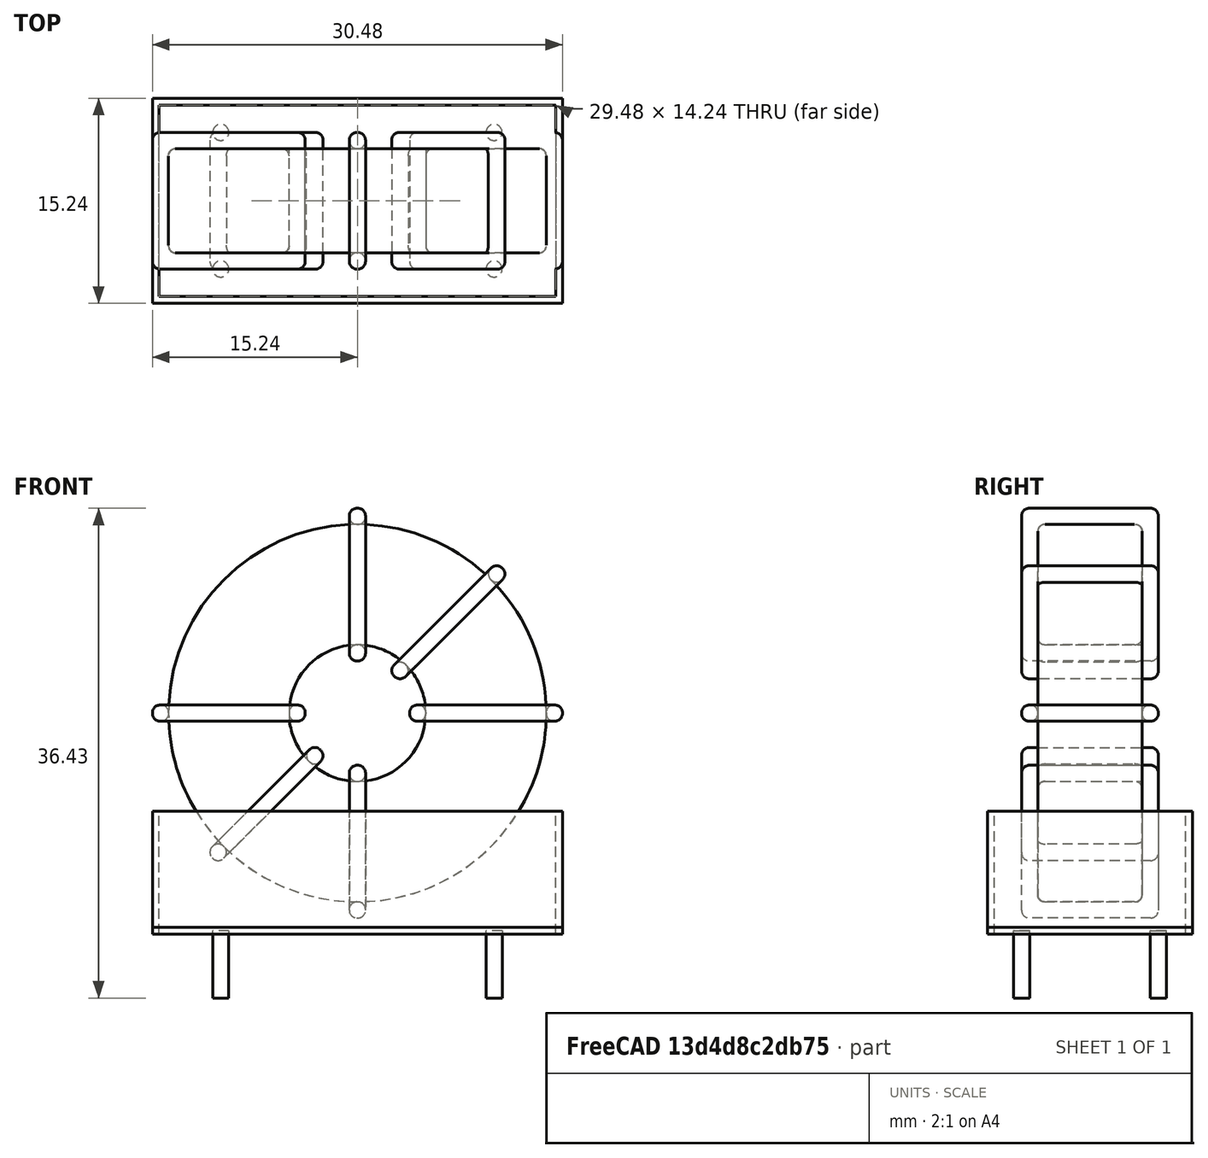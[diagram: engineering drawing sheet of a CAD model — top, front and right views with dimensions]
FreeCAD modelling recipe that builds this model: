
FCSTD DOCUMENT  (FreeCAD 0.16R6703 (Git))
Label: L_CommonModeChoke_Toroid_Vertical_L30.5mm_W15.2mm_Px10.16mm_Py20.32mm_Bourns_8100series
License: All rights reserved
LicenseURL: http://en.wikipedia.org/wiki/All_rights_reserved
objects: Sketcher::SketchObject×8, PartDesign::Pad×8, PartDesign::Fillet×5, Spreadsheet::Sheet×1
note: 29 computed .brp shape members not serialized (recipe doc carries the construction recipe); baked Part::Feature solids carry a one-line shape summary decoded from their .brp

FEATURE [Spreadsheet::Sheet] Spreadsheet  label="dimensions"
  cells = A1=Wx; B1(Wx)=30.48; C1(WW)=10.16; D1(iWx)=30.48; A2=Wy; B2(Wy)=10.16; D2(iWy)=15.24; A3=RM; B3(RMx)=10.16; C3(RMy)=20.32; A4=d_wire; B4(d_wire)=1.2; A5=H; B5(H)=31; A6=offsetx; B6(offsetx)=5.079999999999998
FEATURE [Sketcher::SketchObject] Sketch
  Placement = pos=(10.16,-5.08,0) rot=(1,0,0;1.5708rad)
  expr: Placement.Base.x = Spreadsheet.RMy / 2
  expr: Constraints[4] = Spreadsheet.WW / 2
  expr: Placement.Base.y = -Spreadsheet.RMx / 2
  expr: Constraints[0] = Spreadsheet.Wx / 2 - Spreadsheet.d_wire
  expr: Constraints[2] = Spreadsheet.Wx / 2 + Spreadsheet.d_wire + 0.5
  sketch-geometry (2):
    g0: Circle CenterX=0 CenterY=16.94 CenterZ=0 NormalX=0 NormalY=0 NormalZ=1 Radius=14.04
    g1: Circle CenterX=0 CenterY=16.94 CenterZ=0 NormalX=0 NormalY=0 NormalZ=1 Radius=5.08
  constraints (5):
    c: Radius(g0) = 14.04
    c: DistanceX(g-1,g0) = 0
    c: DistanceY(g-1,g0) = 16.94
    c: Coincident(g1,g0)
    c: Radius(g1) = 5.08
FEATURE [PartDesign::Pad] Pad
  Length = 7.76
  Length2 = 100
  Midplane = true
  Placement = pos=(10.16,-5.08,0) rot=(1,0,0;1.5708rad)
  Sketch = -> Sketch
  Type = 0
  expr: Length = Spreadsheet.Wy - 2 * Spreadsheet.d_wire
FEATURE [Sketcher::SketchObject] Sketch001
  Placement = pos=(0,0,0.75) rot=(0,0,1;0rad)
  expr: Constraints[4] = Spreadsheet.RMy
  expr: Constraints[2] = -Spreadsheet.RMx
  expr: Constraints[1] = Spreadsheet.d_wire / 2
  sketch-geometry (4):
    g0: Circle CenterX=0 CenterY=0 CenterZ=0 NormalX=0 NormalY=0 NormalZ=1 Radius=0.6
    g1: Circle CenterX=20.32 CenterY=-10.16 CenterZ=0 NormalX=0 NormalY=0 NormalZ=1 Radius=0.6
    g2: Circle CenterX=0 CenterY=-10.16 CenterZ=0 NormalX=0 NormalY=0 NormalZ=1 Radius=0.6
    g3: Circle CenterX=20.32 CenterY=0 CenterZ=0 NormalX=0 NormalY=0 NormalZ=1 Radius=0.6
  constraints (11):
    c: Equal(g0,g1)
    c: Radius(g0) = 0.6
    c: DistanceY(g-1,g1) = -10.16
    c: Coincident(g0,g-1)
    c: DistanceX(g-1,g1) = 20.32
    c: PointOnObject(g2,g-2)
    c: DistanceY(g-1,g3) = 0
    c: DistanceY(g2,g1) = 0
    c: DistanceX(g3,g1) = 0
    c: Equal(g3,g2)
    c: Equal(g2,g1)
FEATURE [PartDesign::Pad] Pad001
  Length = 5
  Length2 = 0
  Placement = pos=(0,0,0.75) rot=(0,0,1;0rad)
  Reversed = true
  Sketch = -> Sketch001
  Type = 0
FEATURE [PartDesign::Fillet] Fillet
  Base = -> Pad [Edge6,Edge3,Edge2]
  Placement = pos=(10.16,-5.08,0) rot=(1,0,0;1.5708rad)
  Radius = 0.5
FEATURE [Sketcher::SketchObject] Sketch003
  Placement = pos=(10.16,0,16.94) rot=(1,0,0;3.14159rad)
  expr: Placement.Base.x = Spreadsheet.RMy / 2
  expr: Constraints[18] = Spreadsheet.d_wire
  expr: Constraints[16] = Spreadsheet.d_wire
  expr: Constraints[19] = Spreadsheet.d_wire
  expr: Constraints[17] = Spreadsheet.d_wire
  expr: Placement.Base.y = -1 * (Spreadsheet.RMx - Spreadsheet.Wy) / 2
  expr: Constraints[21] = (Spreadsheet.Wx - Spreadsheet.WW) / 2 - Spreadsheet.d_wire
  expr: Constraints[22] = Spreadsheet.Wx / 2 - Spreadsheet.d_wire
  expr: Constraints[43] = Spreadsheet.d_wire
  expr: Constraints[48] = Spreadsheet.Wx - Spreadsheet.d_wire * 2
  expr: Constraints[49] = Spreadsheet.Wy
  expr: Placement.Base.z = Spreadsheet.Wx / 2 + Spreadsheet.d_wire + 0.5
  sketch-geometry (16):
    g0: LineSegment StartX=-3.88 StartY=0 StartZ=0 EndX=-15.24 EndY=0 EndZ=0
    g1: LineSegment StartX=-15.24 StartY=0 StartZ=0 EndX=-15.24 EndY=10.16 EndZ=0
    g2: LineSegment StartX=-15.24 StartY=10.16 StartZ=0 EndX=-3.88 EndY=10.16 EndZ=0
    g3: LineSegment StartX=-3.88 StartY=10.16 StartZ=0 EndX=-3.88 EndY=0 EndZ=0
    g4: LineSegment StartX=-14.04 StartY=8.96 StartZ=0 EndX=-5.08 EndY=8.96 EndZ=0
    g5: LineSegment StartX=-5.08 StartY=8.96 StartZ=0 EndX=-5.08 EndY=1.2 EndZ=0
    g6: LineSegment StartX=-5.08 StartY=1.2 StartZ=0 EndX=-14.04 EndY=1.2 EndZ=0
    g7: LineSegment StartX=-14.04 StartY=1.2 StartZ=0 EndX=-14.04 EndY=8.96 EndZ=0
    g8: LineSegment StartX=3.88 StartY=10.16 StartZ=0 EndX=15.24 EndY=10.16 EndZ=0
    g9: LineSegment StartX=15.24 StartY=10.16 StartZ=0 EndX=15.24 EndY=0 EndZ=0
    g10: LineSegment StartX=15.24 StartY=0 StartZ=0 EndX=3.88 EndY=0 EndZ=0
    g11: LineSegment StartX=3.88 StartY=0 StartZ=0 EndX=3.88 EndY=10.16 EndZ=0
    g12: LineSegment StartX=5.08 StartY=8.96 StartZ=0 EndX=14.04 EndY=8.96 EndZ=0
    g13: LineSegment StartX=14.04 StartY=8.96 StartZ=0 EndX=14.04 EndY=1.2 EndZ=0
    g14: LineSegment StartX=14.04 StartY=1.2 StartZ=0 EndX=5.08 EndY=1.2 EndZ=0
    g15: LineSegment StartX=5.08 StartY=1.2 StartZ=0 EndX=5.08 EndY=8.96 EndZ=0
  constraints (50):
    c: Horizontal(g0)
    c: Coincident(g1,g0)
    c: Vertical(g1)
    c: Coincident(g2,g1)
    c: Horizontal(g2)
    c: Coincident(g3,g2)
    c: Coincident(g3,g0)
    c: Vertical(g3)
    c: Coincident(g4,g5)
    c: Coincident(g5,g6)
    c: Coincident(g6,g7)
    c: Coincident(g7,g4)
    c: Horizontal(g4)
    c: Horizontal(g6)
    c: Vertical(g5)
    c: Vertical(g7)
    c: DistanceX(g1,g4) = 1.2
    c: DistanceY(g4,g1) = 1.2
    c: DistanceX(g5,g0) = 1.2
    c: DistanceY(g0,g5) = 1.2
    c: DistanceY(g-1,g0) = 0
    c: DistanceX(g6,g6) = 8.96
    c: DistanceX(g6,g-1) = 14.04
    c: Coincident(g8,g9)
    c: Coincident(g9,g10)
    c: Coincident(g10,g11)
    c: Coincident(g11,g8)
    c: Horizontal(g8)
    c: Horizontal(g10)
    c: Vertical(g9)
    c: Vertical(g11)
    c: Coincident(g12,g13)
    c: Coincident(g13,g14)
    c: Coincident(g14,g15)
    c: Coincident(g15,g12)
    c: Horizontal(g12)
    c: Horizontal(g14)
    c: Vertical(g13)
    c: Vertical(g15)
    c: DistanceY(g8,g2) = 0
    c: DistanceY(g10,g0) = 0
    c: DistanceY(g14,g5) = 0
    c: DistanceY(g12,g4) = 0
    c: DistanceX(g8,g12) = 1.2
    c: Equal(g8,g2)
    c: Equal(g12,g4)
    c: Equal(g9,g1)
    c: Equal(g13,g7)
    c: DistanceX(g4,g12) = 28.08
    c: DistanceY(g0,g1) = 10.16
FEATURE [PartDesign::Pad] Pad002
  Length = 1.2
  Length2 = 100
  Midplane = true
  Placement = pos=(10.16,0,16.94) rot=(1,0,0;3.14159rad)
  Sketch = -> Sketch003
  Type = 0
  expr: Length = Spreadsheet.d_wire
FEATURE [PartDesign::Fillet] Fillet001
  Base = -> Pad002 [Edge38,Edge41,Edge42,Edge43,Edge29,Edge32,Edge33,Edge34,Edge25,Edge35,Edge36,Edge13,Edge14,Edge15,Edge16,Edge17,Edge18,Edge19,Edge1,Edge2,Edge3,Edge4,Edge5,Edge6,Edge7,Edge37,Edge39,Edge40,Edge20,Edge23,Edge24,Edge21,Edge22,Edge8,Edge9,Edge10,Edge11,Edge12,Edge26,Edge27,+8 more]
  Placement = pos=(10.16,0,16.94) rot=(1,0,0;3.14159rad)
  Radius = 0.564
  expr: Radius = Spreadsheet.d_wire * 0.47
FEATURE [Sketcher::SketchObject] Sketch004
  Placement = pos=(10.16,0,16.94) rot=(0.92388,0,0.382683;3.14159rad)
  expr: Placement.Base.x = Spreadsheet.RMy / 2
  expr: Constraints[18] = Spreadsheet.d_wire
  expr: Constraints[16] = Spreadsheet.d_wire
  expr: Constraints[19] = Spreadsheet.d_wire
  expr: Constraints[17] = Spreadsheet.d_wire
  expr: Placement.Base.y = -1 * (Spreadsheet.RMx - Spreadsheet.Wy) / 2
  expr: Constraints[21] = (Spreadsheet.Wx - Spreadsheet.WW) / 2 - Spreadsheet.d_wire
  expr: Constraints[22] = Spreadsheet.Wx / 2 - Spreadsheet.d_wire
  expr: Constraints[43] = Spreadsheet.d_wire
  expr: Constraints[48] = Spreadsheet.Wx - 2 * Spreadsheet.d_wire
  expr: Constraints[49] = Spreadsheet.Wy
  expr: Placement.Base.z = Spreadsheet.Wx / 2 + Spreadsheet.d_wire + 0.5
  sketch-geometry (16):
    g0: LineSegment StartX=-3.88 StartY=0 StartZ=0 EndX=-15.24 EndY=0 EndZ=0
    g1: LineSegment StartX=-15.24 StartY=0 StartZ=0 EndX=-15.24 EndY=10.16 EndZ=0
    g2: LineSegment StartX=-15.24 StartY=10.16 StartZ=0 EndX=-3.88 EndY=10.16 EndZ=0
    g3: LineSegment StartX=-3.88 StartY=10.16 StartZ=0 EndX=-3.88 EndY=0 EndZ=0
    g4: LineSegment StartX=-14.04 StartY=8.96 StartZ=0 EndX=-5.08 EndY=8.96 EndZ=0
    g5: LineSegment StartX=-5.08 StartY=8.96 StartZ=0 EndX=-5.08 EndY=1.2 EndZ=0
    g6: LineSegment StartX=-5.08 StartY=1.2 StartZ=0 EndX=-14.04 EndY=1.2 EndZ=0
    g7: LineSegment StartX=-14.04 StartY=1.2 StartZ=0 EndX=-14.04 EndY=8.96 EndZ=0
    g8: LineSegment StartX=3.88 StartY=10.16 StartZ=0 EndX=15.24 EndY=10.16 EndZ=0
    g9: LineSegment StartX=15.24 StartY=10.16 StartZ=0 EndX=15.24 EndY=0 EndZ=0
    g10: LineSegment StartX=15.24 StartY=0 StartZ=0 EndX=3.88 EndY=0 EndZ=0
    g11: LineSegment StartX=3.88 StartY=0 StartZ=0 EndX=3.88 EndY=10.16 EndZ=0
    g12: LineSegment StartX=5.08 StartY=8.96 StartZ=0 EndX=14.04 EndY=8.96 EndZ=0
    g13: LineSegment StartX=14.04 StartY=8.96 StartZ=0 EndX=14.04 EndY=1.2 EndZ=0
    g14: LineSegment StartX=14.04 StartY=1.2 StartZ=0 EndX=5.08 EndY=1.2 EndZ=0
    g15: LineSegment StartX=5.08 StartY=1.2 StartZ=0 EndX=5.08 EndY=8.96 EndZ=0
  constraints (50):
    c: Horizontal(g0)
    c: Coincident(g1,g0)
    c: Vertical(g1)
    c: Coincident(g2,g1)
    c: Horizontal(g2)
    c: Coincident(g3,g2)
    c: Coincident(g3,g0)
    c: Vertical(g3)
    c: Coincident(g4,g5)
    c: Coincident(g5,g6)
    c: Coincident(g6,g7)
    c: Coincident(g7,g4)
    c: Horizontal(g4)
    c: Horizontal(g6)
    c: Vertical(g5)
    c: Vertical(g7)
    c: DistanceX(g1,g4) = 1.2
    c: DistanceY(g4,g1) = 1.2
    c: DistanceX(g5,g0) = 1.2
    c: DistanceY(g0,g5) = 1.2
    c: DistanceY(g-1,g0) = 0
    c: DistanceX(g6,g6) = 8.96
    c: DistanceX(g6,g-1) = 14.04
    c: Coincident(g8,g9)
    c: Coincident(g9,g10)
    c: Coincident(g10,g11)
    c: Coincident(g11,g8)
    c: Horizontal(g8)
    c: Horizontal(g10)
    c: Vertical(g9)
    c: Vertical(g11)
    c: Coincident(g12,g13)
    c: Coincident(g13,g14)
    c: Coincident(g14,g15)
    c: Coincident(g15,g12)
    c: Horizontal(g12)
    c: Horizontal(g14)
    c: Vertical(g13)
    c: Vertical(g15)
    c: DistanceY(g8,g2) = 0
    c: DistanceY(g10,g0) = 0
    c: DistanceY(g14,g5) = 0
    c: DistanceY(g12,g4) = 0
    c: DistanceX(g8,g12) = 1.2
    c: Equal(g8,g2)
    c: Equal(g12,g4)
    c: Equal(g9,g1)
    c: Equal(g13,g7)
    c: DistanceX(g4,g12) = 28.08
    c: DistanceY(g0,g1) = 10.16
FEATURE [PartDesign::Pad] Pad003
  Length = 1.2
  Length2 = 100
  Midplane = true
  Placement = pos=(10.16,0,16.94) rot=(0.92388,0,0.382683;3.14159rad)
  Sketch = -> Sketch004
  Type = 0
  expr: Length = Spreadsheet.d_wire
FEATURE [PartDesign::Fillet] Fillet002
  Base = -> Pad003 [Edge38,Edge41,Edge42,Edge43,Edge29,Edge32,Edge33,Edge34,Edge25,Edge35,Edge36,Edge13,Edge14,Edge15,Edge16,Edge17,Edge18,Edge19,Edge1,Edge2,Edge3,Edge4,Edge5,Edge6,Edge7,Edge37,Edge39,Edge40,Edge20,Edge23,Edge24,Edge21,Edge22,Edge8,Edge9,Edge10,Edge11,Edge12,Edge26,Edge27,+8 more]
  Placement = pos=(10.16,0,16.94) rot=(0.92388,0,0.382683;3.14159rad)
  Radius = 0.564
  expr: Radius = Spreadsheet.d_wire * 0.47
FEATURE [Sketcher::SketchObject] Sketch005
  Placement = pos=(10.16,0,16.94) rot=(0.92388,0,-0.382683;3.14159rad)
  expr: Placement.Base.x = Spreadsheet.RMy / 2
  expr: Constraints[18] = Spreadsheet.d_wire
  expr: Constraints[16] = Spreadsheet.d_wire
  expr: Constraints[19] = Spreadsheet.d_wire
  expr: Constraints[17] = Spreadsheet.d_wire
  expr: Placement.Base.y = -1 * (Spreadsheet.RMx - Spreadsheet.Wy) / 2
  expr: Constraints[21] = (Spreadsheet.Wx - Spreadsheet.WW) / 2 - Spreadsheet.d_wire
  expr: Constraints[22] = Spreadsheet.Wx / 2 - Spreadsheet.d_wire
  expr: Constraints[43] = Spreadsheet.d_wire
  expr: Constraints[48] = Spreadsheet.Wx - 2 * Spreadsheet.d_wire
  expr: Constraints[49] = Spreadsheet.Wy
  expr: Placement.Base.z = Spreadsheet.Wx / 2 + Spreadsheet.d_wire + 0.5
  sketch-geometry (16):
    g0: LineSegment StartX=-3.88 StartY=0 StartZ=0 EndX=-15.24 EndY=0 EndZ=0
    g1: LineSegment StartX=-15.24 StartY=0 StartZ=0 EndX=-15.24 EndY=10.16 EndZ=0
    g2: LineSegment StartX=-15.24 StartY=10.16 StartZ=0 EndX=-3.88 EndY=10.16 EndZ=0
    g3: LineSegment StartX=-3.88 StartY=10.16 StartZ=0 EndX=-3.88 EndY=0 EndZ=0
    g4: LineSegment StartX=-14.04 StartY=8.96 StartZ=0 EndX=-5.08 EndY=8.96 EndZ=0
    g5: LineSegment StartX=-5.08 StartY=8.96 StartZ=0 EndX=-5.08 EndY=1.2 EndZ=0
    g6: LineSegment StartX=-5.08 StartY=1.2 StartZ=0 EndX=-14.04 EndY=1.2 EndZ=0
    g7: LineSegment StartX=-14.04 StartY=1.2 StartZ=0 EndX=-14.04 EndY=8.96 EndZ=0
    g8: LineSegment StartX=3.88 StartY=10.16 StartZ=0 EndX=15.24 EndY=10.16 EndZ=0
    g9: LineSegment StartX=15.24 StartY=10.16 StartZ=0 EndX=15.24 EndY=0 EndZ=0
    g10: LineSegment StartX=15.24 StartY=0 StartZ=0 EndX=3.88 EndY=0 EndZ=0
    g11: LineSegment StartX=3.88 StartY=0 StartZ=0 EndX=3.88 EndY=10.16 EndZ=0
    g12: LineSegment StartX=5.08 StartY=8.96 StartZ=0 EndX=14.04 EndY=8.96 EndZ=0
    g13: LineSegment StartX=14.04 StartY=8.96 StartZ=0 EndX=14.04 EndY=1.2 EndZ=0
    g14: LineSegment StartX=14.04 StartY=1.2 StartZ=0 EndX=5.08 EndY=1.2 EndZ=0
    g15: LineSegment StartX=5.08 StartY=1.2 StartZ=0 EndX=5.08 EndY=8.96 EndZ=0
  constraints (50):
    c: Horizontal(g0)
    c: Coincident(g1,g0)
    c: Vertical(g1)
    c: Coincident(g2,g1)
    c: Horizontal(g2)
    c: Coincident(g3,g2)
    c: Coincident(g3,g0)
    c: Vertical(g3)
    c: Coincident(g4,g5)
    c: Coincident(g5,g6)
    c: Coincident(g6,g7)
    c: Coincident(g7,g4)
    c: Horizontal(g4)
    c: Horizontal(g6)
    c: Vertical(g5)
    c: Vertical(g7)
    c: DistanceX(g1,g4) = 1.2
    c: DistanceY(g4,g1) = 1.2
    c: DistanceX(g5,g0) = 1.2
    c: DistanceY(g0,g5) = 1.2
    c: DistanceY(g-1,g0) = 0
    c: DistanceX(g6,g6) = 8.96
    c: DistanceX(g6,g-1) = 14.04
    c: Coincident(g8,g9)
    c: Coincident(g9,g10)
    c: Coincident(g10,g11)
    c: Coincident(g11,g8)
    c: Horizontal(g8)
    c: Horizontal(g10)
    c: Vertical(g9)
    c: Vertical(g11)
    c: Coincident(g12,g13)
    c: Coincident(g13,g14)
    c: Coincident(g14,g15)
    c: Coincident(g15,g12)
    c: Horizontal(g12)
    c: Horizontal(g14)
    c: Vertical(g13)
    c: Vertical(g15)
    c: DistanceY(g8,g2) = 0
    c: DistanceY(g10,g0) = 0
    c: DistanceY(g14,g5) = 0
    c: DistanceY(g12,g4) = 0
    c: DistanceX(g8,g12) = 1.2
    c: Equal(g8,g2)
    c: Equal(g12,g4)
    c: Equal(g9,g1)
    c: Equal(g13,g7)
    c: DistanceX(g4,g12) = 28.08
    c: DistanceY(g0,g1) = 10.16
FEATURE [PartDesign::Pad] Pad004
  Length = 1.2
  Length2 = 100
  Midplane = true
  Placement = pos=(10.16,0,16.94) rot=(0.92388,0,-0.382683;3.14159rad)
  Sketch = -> Sketch005
  Type = 0
  expr: Length = Spreadsheet.d_wire
FEATURE [PartDesign::Fillet] Fillet003
  Base = -> Pad004 [Edge38,Edge41,Edge42,Edge43,Edge29,Edge32,Edge33,Edge34,Edge25,Edge35,Edge36,Edge13,Edge14,Edge15,Edge16,Edge17,Edge18,Edge19,Edge1,Edge2,Edge3,Edge4,Edge5,Edge6,Edge7,Edge37,Edge39,Edge40,Edge20,Edge23,Edge24,Edge21,Edge22,Edge8,Edge9,Edge10,Edge11,Edge12,Edge26,Edge27,+8 more]
  Placement = pos=(10.16,0,16.94) rot=(0.92388,0,-0.382683;3.14159rad)
  Radius = 0.564
  expr: Radius = Spreadsheet.d_wire * 0.47
FEATURE [Sketcher::SketchObject] Sketch006
  Placement = pos=(10.16,0,16.94) rot=(0.707107,0,0.707107;3.14159rad)
  expr: Placement.Base.x = Spreadsheet.RMy / 2
  expr: Constraints[18] = Spreadsheet.d_wire
  expr: Constraints[16] = Spreadsheet.d_wire
  expr: Constraints[19] = Spreadsheet.d_wire
  expr: Constraints[17] = Spreadsheet.d_wire
  expr: Placement.Base.y = -1 * (Spreadsheet.RMx - Spreadsheet.Wy) / 2
  expr: Constraints[21] = (Spreadsheet.Wx - Spreadsheet.WW) / 2 - Spreadsheet.d_wire
  expr: Constraints[22] = Spreadsheet.Wx / 2 - Spreadsheet.d_wire
  expr: Constraints[43] = Spreadsheet.d_wire
  expr: Constraints[48] = Spreadsheet.Wx - Spreadsheet.d_wire * 2
  expr: Constraints[49] = Spreadsheet.Wy
  expr: Placement.Base.z = Spreadsheet.Wx / 2 + Spreadsheet.d_wire + 0.5
  sketch-geometry (16):
    g0: LineSegment StartX=-3.88 StartY=0 StartZ=0 EndX=-15.24 EndY=0 EndZ=0
    g1: LineSegment StartX=-15.24 StartY=0 StartZ=0 EndX=-15.24 EndY=10.16 EndZ=0
    g2: LineSegment StartX=-15.24 StartY=10.16 StartZ=0 EndX=-3.88 EndY=10.16 EndZ=0
    g3: LineSegment StartX=-3.88 StartY=10.16 StartZ=0 EndX=-3.88 EndY=0 EndZ=0
    g4: LineSegment StartX=-14.04 StartY=8.96 StartZ=0 EndX=-5.08 EndY=8.96 EndZ=0
    g5: LineSegment StartX=-5.08 StartY=8.96 StartZ=0 EndX=-5.08 EndY=1.2 EndZ=0
    g6: LineSegment StartX=-5.08 StartY=1.2 StartZ=0 EndX=-14.04 EndY=1.2 EndZ=0
    g7: LineSegment StartX=-14.04 StartY=1.2 StartZ=0 EndX=-14.04 EndY=8.96 EndZ=0
    g8: LineSegment StartX=3.88 StartY=10.16 StartZ=0 EndX=15.24 EndY=10.16 EndZ=0
    g9: LineSegment StartX=15.24 StartY=10.16 StartZ=0 EndX=15.24 EndY=0 EndZ=0
    g10: LineSegment StartX=15.24 StartY=0 StartZ=0 EndX=3.88 EndY=0 EndZ=0
    g11: LineSegment StartX=3.88 StartY=0 StartZ=0 EndX=3.88 EndY=10.16 EndZ=0
    g12: LineSegment StartX=5.08 StartY=8.96 StartZ=0 EndX=14.04 EndY=8.96 EndZ=0
    g13: LineSegment StartX=14.04 StartY=8.96 StartZ=0 EndX=14.04 EndY=1.2 EndZ=0
    g14: LineSegment StartX=14.04 StartY=1.2 StartZ=0 EndX=5.08 EndY=1.2 EndZ=0
    g15: LineSegment StartX=5.08 StartY=1.2 StartZ=0 EndX=5.08 EndY=8.96 EndZ=0
  constraints (50):
    c: Horizontal(g0)
    c: Coincident(g1,g0)
    c: Vertical(g1)
    c: Coincident(g2,g1)
    c: Horizontal(g2)
    c: Coincident(g3,g2)
    c: Coincident(g3,g0)
    c: Vertical(g3)
    c: Coincident(g4,g5)
    c: Coincident(g5,g6)
    c: Coincident(g6,g7)
    c: Coincident(g7,g4)
    c: Horizontal(g4)
    c: Horizontal(g6)
    c: Vertical(g5)
    c: Vertical(g7)
    c: DistanceX(g1,g4) = 1.2
    c: DistanceY(g4,g1) = 1.2
    c: DistanceX(g5,g0) = 1.2
    c: DistanceY(g0,g5) = 1.2
    c: DistanceY(g-1,g0) = 0
    c: DistanceX(g6,g6) = 8.96
    c: DistanceX(g6,g-1) = 14.04
    c: Coincident(g8,g9)
    c: Coincident(g9,g10)
    c: Coincident(g10,g11)
    c: Coincident(g11,g8)
    c: Horizontal(g8)
    c: Horizontal(g10)
    c: Vertical(g9)
    c: Vertical(g11)
    c: Coincident(g12,g13)
    c: Coincident(g13,g14)
    c: Coincident(g14,g15)
    c: Coincident(g15,g12)
    c: Horizontal(g12)
    c: Horizontal(g14)
    c: Vertical(g13)
    c: Vertical(g15)
    c: DistanceY(g8,g2) = 0
    c: DistanceY(g10,g0) = 0
    c: DistanceY(g14,g5) = 0
    c: DistanceY(g12,g4) = 0
    c: DistanceX(g8,g12) = 1.2
    c: Equal(g8,g2)
    c: Equal(g12,g4)
    c: Equal(g9,g1)
    c: Equal(g13,g7)
    c: DistanceX(g4,g12) = 28.08
    c: DistanceY(g0,g1) = 10.16
FEATURE [PartDesign::Pad] Pad005
  Length = 1.2
  Length2 = 100
  Midplane = true
  Placement = pos=(10.16,0,16.94) rot=(0.707107,0,0.707107;3.14159rad)
  Sketch = -> Sketch006
  Type = 0
  expr: Length = Spreadsheet.d_wire
FEATURE [PartDesign::Fillet] Fillet004
  Base = -> Pad005 [Edge38,Edge41,Edge42,Edge43,Edge29,Edge32,Edge33,Edge34,Edge25,Edge35,Edge36,Edge13,Edge14,Edge15,Edge16,Edge17,Edge18,Edge19,Edge1,Edge2,Edge3,Edge4,Edge5,Edge6,Edge7,Edge37,Edge39,Edge40,Edge20,Edge23,Edge24,Edge21,Edge22,Edge8,Edge9,Edge10,Edge11,Edge12,Edge26,Edge27,+8 more]
  Placement = pos=(10.16,0,16.94) rot=(0.707107,0,0.707107;3.14159rad)
  Radius = 0.564
  expr: Radius = Spreadsheet.d_wire * 0.47
FEATURE [Sketcher::SketchObject] Sketch007
  Placement = pos=(10.16,0,0.5) rot=(0,0,1;0rad)
  expr: Placement.Base.x = Spreadsheet.RMy / 2
  expr: Placement.Base.z = 0.5
  expr: Constraints[11] = Spreadsheet.iWx / 2
  expr: Constraints[10] = (Spreadsheet.iWy - Spreadsheet.RMx) / 2
  expr: Constraints[9] = Spreadsheet.iWy
  expr: Constraints[8] = Spreadsheet.iWx
  sketch-geometry (4):
    g0: LineSegment StartX=-15.24 StartY=2.54 StartZ=0 EndX=15.24 EndY=2.54 EndZ=0
    g1: LineSegment StartX=15.24 StartY=2.54 StartZ=0 EndX=15.24 EndY=-12.7 EndZ=0
    g2: LineSegment StartX=15.24 StartY=-12.7 StartZ=0 EndX=-15.24 EndY=-12.7 EndZ=0
    g3: LineSegment StartX=-15.24 StartY=-12.7 StartZ=0 EndX=-15.24 EndY=2.54 EndZ=0
  constraints (12):
    c: Coincident(g0,g1)
    c: Coincident(g1,g2)
    c: Coincident(g2,g3)
    c: Coincident(g3,g0)
    c: Horizontal(g0)
    c: Horizontal(g2)
    c: Vertical(g1)
    c: Vertical(g3)
    c: DistanceX(g0,g0) = 30.48
    c: DistanceY(g3,g3) = 15.24
    c: DistanceY(g-1,g0) = 2.54
    c: DistanceX(g0,g-1) = 15.24
FEATURE [PartDesign::Pad] Pad006
  Length = 0.5
  Length2 = 100
  Placement = pos=(10.16,0,0.5) rot=(0,0,1;0rad)
  Sketch = -> Sketch007
  Type = 0
FEATURE [Sketcher::SketchObject] Sketch008
  Placement = pos=(10.16,0,0.5) rot=(0,0,1;0rad)
  expr: Placement.Base.x = Spreadsheet.RMy / 2
  expr: Constraints[8] = Spreadsheet.iWx
  expr: Constraints[9] = Spreadsheet.iWy
  expr: Constraints[10] = (Spreadsheet.iWy - Spreadsheet.RMx) / 2
  expr: Placement.Base.z = 0.5
  expr: Constraints[21] = 0.5
  expr: Constraints[11] = Spreadsheet.iWx / 2
  sketch-geometry (8):
    g0: LineSegment StartX=-15.24 StartY=2.54 StartZ=0 EndX=15.24 EndY=2.54 EndZ=0
    g1: LineSegment StartX=15.24 StartY=2.54 StartZ=0 EndX=15.24 EndY=-12.7 EndZ=0
    g2: LineSegment StartX=15.24 StartY=-12.7 StartZ=0 EndX=-15.24 EndY=-12.7 EndZ=0
    g3: LineSegment StartX=-15.24 StartY=-12.7 StartZ=0 EndX=-15.24 EndY=2.54 EndZ=0
    g4: LineSegment StartX=-14.74 StartY=2.04 StartZ=0 EndX=14.74 EndY=2.04 EndZ=0
    g5: LineSegment StartX=14.74 StartY=2.04 StartZ=0 EndX=14.74 EndY=-12.2 EndZ=0
    g6: LineSegment StartX=14.74 StartY=-12.2 StartZ=0 EndX=-14.74 EndY=-12.2 EndZ=0
    g7: LineSegment StartX=-14.74 StartY=-12.2 StartZ=0 EndX=-14.74 EndY=2.04 EndZ=0
  constraints (24):
    c: Coincident(g0,g1)
    c: Coincident(g1,g2)
    c: Coincident(g2,g3)
    c: Coincident(g3,g0)
    c: Horizontal(g0)
    c: Horizontal(g2)
    c: Vertical(g1)
    c: Vertical(g3)
    c: DistanceX(g0,g0) = 30.48
    c: DistanceY(g3,g3) = 15.24
    c: DistanceY(g-1,g0) = 2.54
    c: DistanceX(g0,g-1) = 15.24
    c: Coincident(g4,g5)
    c: Coincident(g5,g6)
    c: Coincident(g6,g7)
    c: Coincident(g7,g4)
    c: Horizontal(g4)
    c: Horizontal(g6)
    c: Vertical(g5)
    c: Vertical(g7)
    c: DistanceX(g5,g1) = 0.5
    c: DistanceY(g1,g5) = 0.5
    c: DistanceX(g0,g4) = 0.5
    c: DistanceY(g4,g0) = 0.5
FEATURE [PartDesign::Pad] Pad007
  Length = 9.144
  Length2 = 100
  Placement = pos=(10.16,0,0.5) rot=(0,0,1;0rad)
  Sketch = -> Sketch008
  Type = 0
  expr: Length = Spreadsheet.Wx * 0.3
